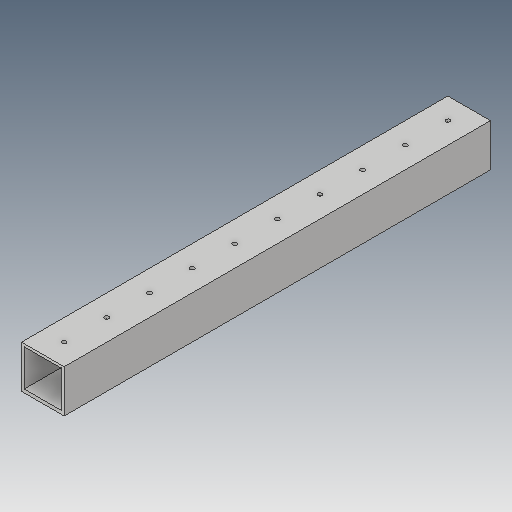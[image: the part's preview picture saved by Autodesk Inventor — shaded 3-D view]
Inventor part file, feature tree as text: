
AUTODESK INVENTOR PART (.ipt)
format: ipt  version: 2018 (Build 220112000, 112)  size: 121,856 bytes
history: native  units: in
note: dims shown in document units (in); Inventor stores cm internally (conversion verified against a paired STEP export)
features: sketch x2, extrude x1, hole x1
ambient origin geometry x8: Origin, YZ Plane, XZ Plane, XY Plane, X Axis, Y Axis, Z Axis, Center Point
bodies: Solid1 (feature_tree)
feature tree (4):
  extrude  "Extrusion1"  Depth=1.0in
  hole  "Hole1"  [1 undecoded]
  sketch  "Sketch1"  dims[d0=1.0in d1=1.0in]
  sketch  "Sketch2"  dims[d2=0.0625in d3=0.0625in d4=10.0in d5=0.0in d6=0.5in d7=0.5in d8=5.9055in d10=1.0in d11=0.3937in d13=1.0in d15=0.1in d16=0.75in d17=0.375in d18=0.25in d19=0.5635in d20=1.0in d21=0.8108in]
note: 1 required parameter value undecoded (feature->parameter linkage not recoverable at this tier; creation-order binding heuristic only, values carry confidence <= 0.55)
